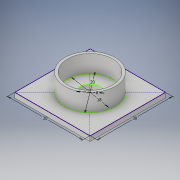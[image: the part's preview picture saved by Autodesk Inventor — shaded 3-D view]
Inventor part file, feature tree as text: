
AUTODESK INVENTOR PART (.ipt)
format: ipt  version: 2019 (Build 230136000, 136)  size: 120,320 bytes
history: native  units: mm
features: extrude x3, other x1, sketch x1
ambient origin geometry x8: Origin, YZ Plane, XZ Plane, XY Plane, X Axis, Y Axis, Z Axis, Center Point
bodies: Body1 (feature_tree)
feature tree (5):
  other  "Sólido1"
  sketch  "Boceto1"  dims[d0=30.0mm d1=30.0mm d4=2.0mm d5=0.0mm d9=18.0mm d12=8.0mm d13=3.0mm d14=0.0mm d15=20.0mm d16=7.0mm d17=0.0mm]
  extrude  "Extrusión1"  Depth=30.0mm
  extrude  "Extrusión4"  Depth=2.0mm TaperAngle=0.0deg
  extrude  "Extrusión5"  Depth=7.0mm
